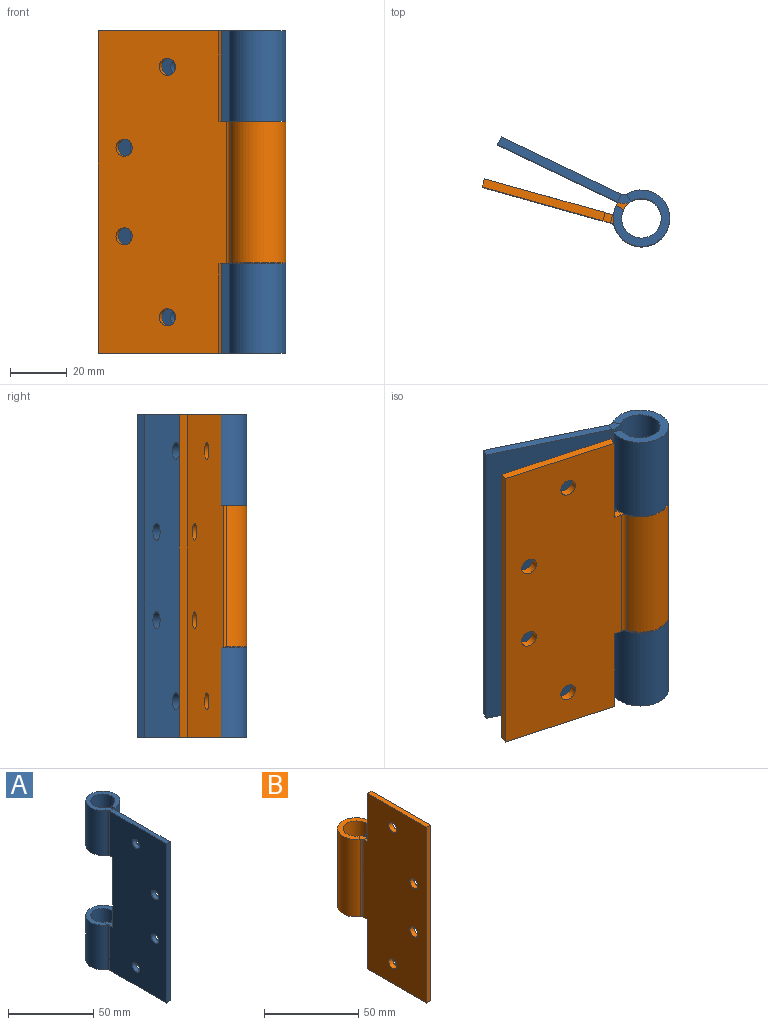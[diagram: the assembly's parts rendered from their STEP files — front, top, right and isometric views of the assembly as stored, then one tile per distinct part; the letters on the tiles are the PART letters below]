
ASSEMBLY  parts=2 mates=1
PART A: 30 faces, bbox 20x67.2x114 mm
  f0: plane 47.06x3mm, normal (0,0,-1), area 141.2mm2, adj f1,f10,f11,f17
  f1: plane 114x3mm, normal (0,-1,0), area 342mm2, adj f0,f2,f10,f11
  f2: plane 47.06x3mm, normal (0,0,1), area 141.2mm2, adj f1,f10,f11,f27
  f3: plane 3x2.5mm, normal (0,0,-1), area 7.5mm2, adj f4,f10,f11,f26
  f4: plane 50x3mm, normal (0,1,0), area 150mm2, adj f3,f5,f10,f11
  f5: plane 3x2.5mm, normal (0,0,1), area 7.5mm2, adj f4,f10,f11,f18
  f6: cylinder r=3mm len=6mm, axis (-1,0,0), area 56.5mm2, adj f10,f11
  f7: cylinder r=3mm len=6mm, axis (-1,0,0), area 56.5mm2, adj f10,f11
  f8: cylinder r=3mm len=6mm, axis (-1,0,0), area 56.5mm2, adj f10,f11
  f9: cylinder r=3mm len=6mm, axis (-1,0,0), area 56.5mm2, adj f10,f11
  f10: plane 114x47.06mm, normal (-1,0,0), area 5127.1mm2, adj f0,f1,f2,f3,f4,f5,f6,f7
  f11: plane 114x47.06mm, normal (1,0,0), area 5127.1mm2, adj f0,f1,f2,f3,f4,f5,f6,f7
  f12: plane 20x20mm, normal (0,0,-1), area 145.8mm2, adj f14,f15,f16,f17
  f13: plane 20x20mm, normal (0,0,1), area 145.8mm2, adj f14,f15,f16,f18
  f14: plane 32x3mm, normal (-1,0.01,0), area 96mm2, adj f12,f13,f15,f16
  f15: cylinder r=10mm len=32mm, axis (0,0,1), area 1830.1mm2, adj f12,f13,f14,f20
  f16: cylinder r=7mm len=32mm, axis (0,0,1), area 1281.1mm2, adj f12,f13,f14,f19
  f17: plane 4.2x3.92mm, normal (0,0,-1), area 10.5mm2, adj f0,f12,f19,f20
  f18: plane 4.2x3.92mm, normal (0,0,1), area 10.5mm2, adj f5,f13,f19,f20
  f19: cylinder r=5mm len=32mm, axis (0,0,-1), area 159.7mm2, adj f11,f16,f17,f18
  f20: cylinder r=2mm len=32mm, axis (0,0,-1), area 63.9mm2, adj f10,f15,f17,f18
  f21: plane 20x20mm, normal (0,0,1), area 145.8mm2, adj f22,f24,f25,f27
  f22: plane 32x3mm, normal (-1,0.01,0), area 96mm2, adj f21,f23,f24,f25
  f23: plane 20x20mm, normal (0,0,-1), area 145.8mm2, adj f22,f24,f25,f26
  f24: cylinder r=10mm len=32mm, axis (0,0,1), area 1830.1mm2, adj f21,f22,f23,f29
  f25: cylinder r=7mm len=32mm, axis (0,0,1), area 1281.1mm2, adj f21,f22,f23,f28
  f26: plane 4.2x3.92mm, normal (0,0,-1), area 10.5mm2, adj f3,f23,f28,f29
  f27: plane 4.2x3.92mm, normal (0,0,1), area 10.5mm2, adj f2,f21,f28,f29
  f28: cylinder r=5mm len=32mm, axis (0,0,-1), area 159.7mm2, adj f11,f25,f26,f27
  f29: cylinder r=2mm len=32mm, axis (0,0,-1), area 63.9mm2, adj f10,f24,f26,f27
PART B: 22 faces, bbox 20x67.2x114 mm
  f0: plane 3x2.79mm, normal (0,0,1), area 8.4mm2, adj f10,f11,f12,f19
  f1: plane 3x2.79mm, normal (0,0,-1), area 8.4mm2, adj f2,f11,f12,f18
  f2: plane 32.12x3mm, normal (0,1,0), area 96.3mm2, adj f1,f3,f11,f12
  f3: plane 44.27x3mm, normal (0,0,-1), area 132.8mm2, adj f2,f4,f11,f12
  f4: plane 114x3mm, normal (0,-1,0), area 342mm2, adj f3,f5,f11,f12
  f5: plane 44.27x3mm, normal (0,0,1), area 132.8mm2, adj f4,f10,f11,f12
  f6: cylinder r=3mm len=6mm, axis (-1,0,0), area 56.5mm2, adj f11,f12
  f7: cylinder r=3mm len=6mm, axis (-1,0,0), area 56.5mm2, adj f11,f12
  f8: cylinder r=3mm len=6mm, axis (-1,0,0), area 56.5mm2, adj f11,f12
  f9: cylinder r=3mm len=6mm, axis (-1,0,0), area 56.5mm2, adj f11,f12
  f10: plane 31.58x3mm, normal (0,1,0), area 94.8mm2, adj f0,f5,f11,f12
  f11: plane 114x47.06mm, normal (-1,0,0), area 5074.3mm2, adj f0,f1,f2,f3,f4,f5,f6,f7
  f12: plane 114x47.06mm, normal (1,0,0), area 5074.3mm2, adj f0,f1,f2,f3,f4,f5,f6,f7
  f13: plane 20x20mm, normal (0,0,-1), area 145.8mm2, adj f15,f16,f17,f18
  f14: plane 20x20mm, normal (0,0,1), area 145.8mm2, adj f15,f16,f17,f19
  f15: plane 50.3x3mm, normal (-1,0.01,0), area 150.9mm2, adj f13,f14,f16,f17
  f16: cylinder r=10mm len=50.3mm, axis (0,0,1), area 2876.7mm2, adj f13,f14,f15,f21
  f17: cylinder r=7mm len=50.3mm, axis (0,0,1), area 2013.7mm2, adj f13,f14,f15,f20
  f18: plane 4.2x3.92mm, normal (0,0,-1), area 10.5mm2, adj f1,f13,f20,f21
  f19: plane 4.2x3.92mm, normal (0,0,1), area 10.5mm2, adj f0,f14,f20,f21
  f20: cylinder r=5mm len=50.3mm, axis (0,0,-1), area 251.1mm2, adj f12,f17,f18,f19
  f21: cylinder r=2mm len=50.3mm, axis (0,0,-1), area 100.4mm2, adj f11,f16,f18,f19
PLACE A rot(axis=(0,0,-1),115.6deg) t=(-26.49,-72.2,-31.09)mm
PLACE B rot(axis=(0.8,0.6,0),180deg) t=(-26.49,-72.2,-31.13)mm
MATE revolute B.f16 <-> A.f15  axis (0,0,1) through (-26.49,-72.2,-6.24)mm
